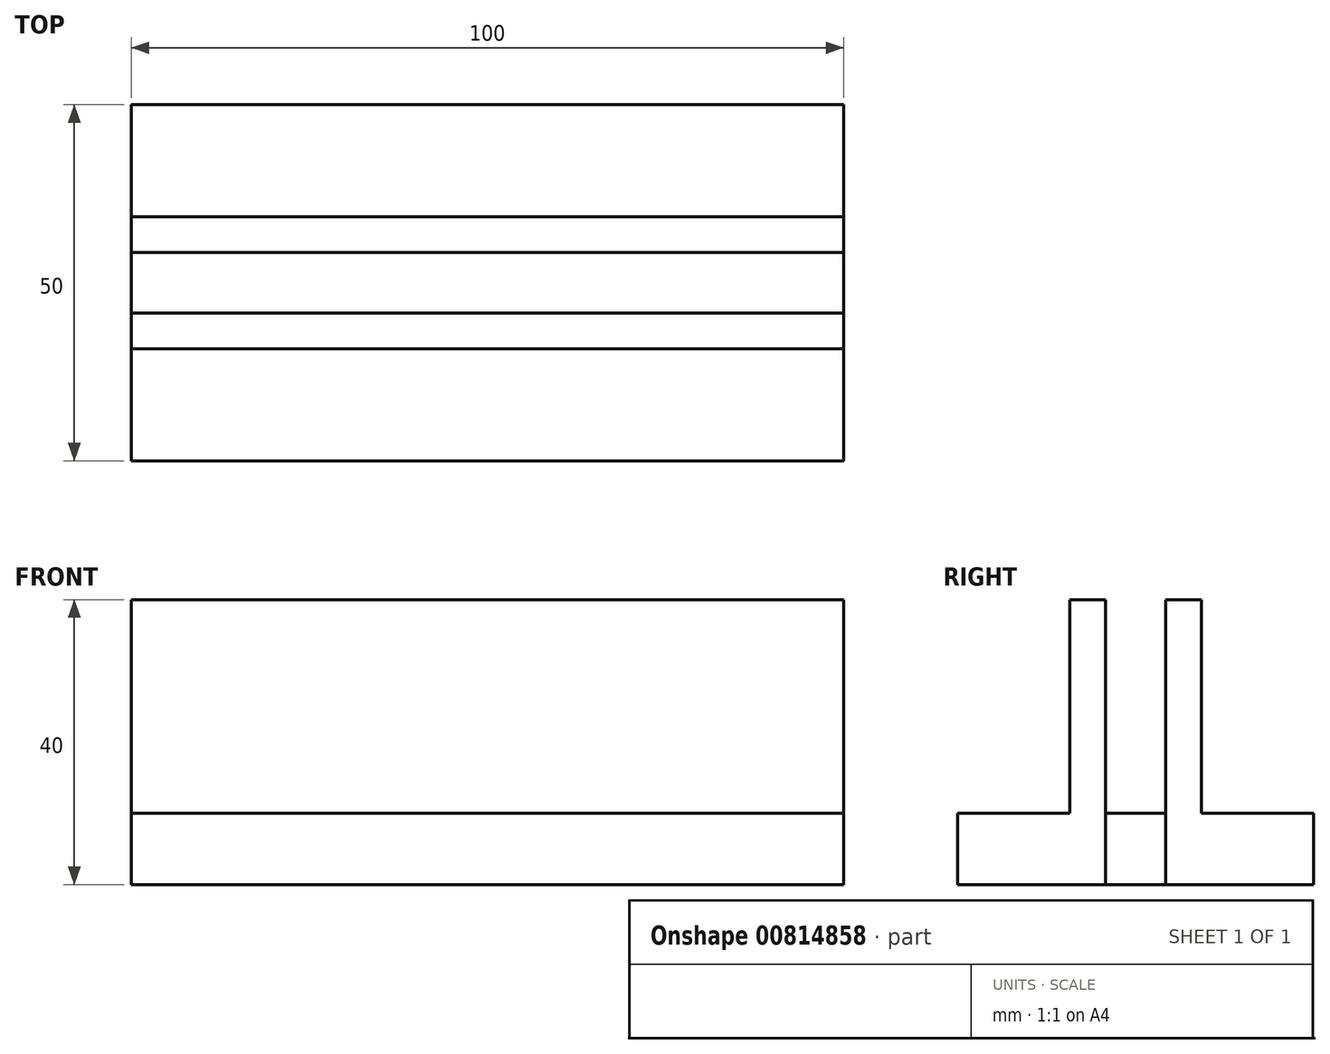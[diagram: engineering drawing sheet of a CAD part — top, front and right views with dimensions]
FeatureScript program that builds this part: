
annotation { "Feature Type Name" : "Feature", "Feature Type Description" : "" }
export const myFeature = defineFeature(function(context is Context, id is Id, definition is map)
    precondition{}
    {
        {
            var Q0;
            Q0=qCreatedBy(makeId("Top.planeOp"),FACE);
            var sketch = newSketch(context, id + "F0", { "sketchPlane" : qUnion([Q0])});
            skLineSegment(sketch, "E0.bottom", {"start": v(50, -25) * mm, "end": v(-50, -25) * mm});
            skLineSegment(sketch, "E0.top", {"start": v(50, 25) * mm, "end": v(-50, 25) * mm});
            skLineSegment(sketch, "E0.left", {"start": v(50, -25) * mm, "end": v(50, 25) * mm});
            skLineSegment(sketch, "E0.right", {"start": v(-50, -25) * mm, "end": v(-50, 25) * mm});
            skPoint(sketch, "E0.middle", {"position": v(0, 0) * mm});
            skSolve(sketch);
        }
        {
            var Q0;
            Q0 = qSketchRegion(id + "F0", true);
            extrude(context, id + "F1", {"entities" : qUnion([Q0]), "depth" : 10 * mm, "offsetDistance" : 25 * mm});
        }
        {
            var Q0;
            Q0=qCreatedBy(makeId("Top.planeOp"),FACE);
            var sketch = newSketch(context, id + "F2", { "sketchPlane" : qUnion([Q0])});
            skLineSegment(sketch, "E1.bottom", {"start": v(50, -9.25) * mm, "end": v(-50, -9.25) * mm});
            skLineSegment(sketch, "E1.top", {"start": v(50, 9.25) * mm, "end": v(-50, 9.25) * mm});
            skLineSegment(sketch, "E1.left", {"start": v(50, -9.25) * mm, "end": v(50, 9.25) * mm});
            skLineSegment(sketch, "E1.right", {"start": v(-50, -9.25) * mm, "end": v(-50, 9.25) * mm});
            skPoint(sketch, "E1.middle", {"position": v(0, 0) * mm});
            skPoint(sketch, "E2.middle", {"position": v(-1.7, -0.65) * mm});
            skSolve(sketch);
        }
        {
            var Q0;
            Q0 = qSketchRegion(id + "F2", true);
            extrude(context, id + "F3", {"entities" : qUnion([Q0]), "operationType" : NewBodyOperationType.ADD, "depth" : 40 * mm, "offsetDistance" : 25 * mm});
        }
        {
            var Q0;
            Q0=qCreatedBy(makeId("Top.planeOp"),FACE);
            var sketch = newSketch(context, id + "F4", { "sketchPlane" : qUnion([Q0])});
            skLineSegment(sketch, "E3.bottom", {"start": v(50, -4.25) * mm, "end": v(-50, -4.25) * mm});
            skLineSegment(sketch, "E3.top", {"start": v(50, 4.25) * mm, "end": v(-50, 4.25) * mm});
            skLineSegment(sketch, "E3.left", {"start": v(50, -4.25) * mm, "end": v(50, 4.25) * mm});
            skLineSegment(sketch, "E3.right", {"start": v(-50, -4.25) * mm, "end": v(-50, 4.25) * mm});
            skPoint(sketch, "E3.middle", {"position": v(0, 0) * mm});
            skSolve(sketch);
        }
        {
            var Q0;
            Q0 = qSketchRegion(id + "F4", true);
            extrude(context, id + "F5", {"entities" : qUnion([Q0]), "operationType" : NewBodyOperationType.REMOVE, "depth" : 40 * mm, "offsetDistance" : 25 * mm});
        }
        {
            var Q0;
            Q0 = qSketchRegion(id + "F4", true);
            extrude(context, id + "F6", {"entities" : qUnion([Q0]), "depth" : 10 * mm, "offsetDistance" : 25 * mm});
        }
    });
